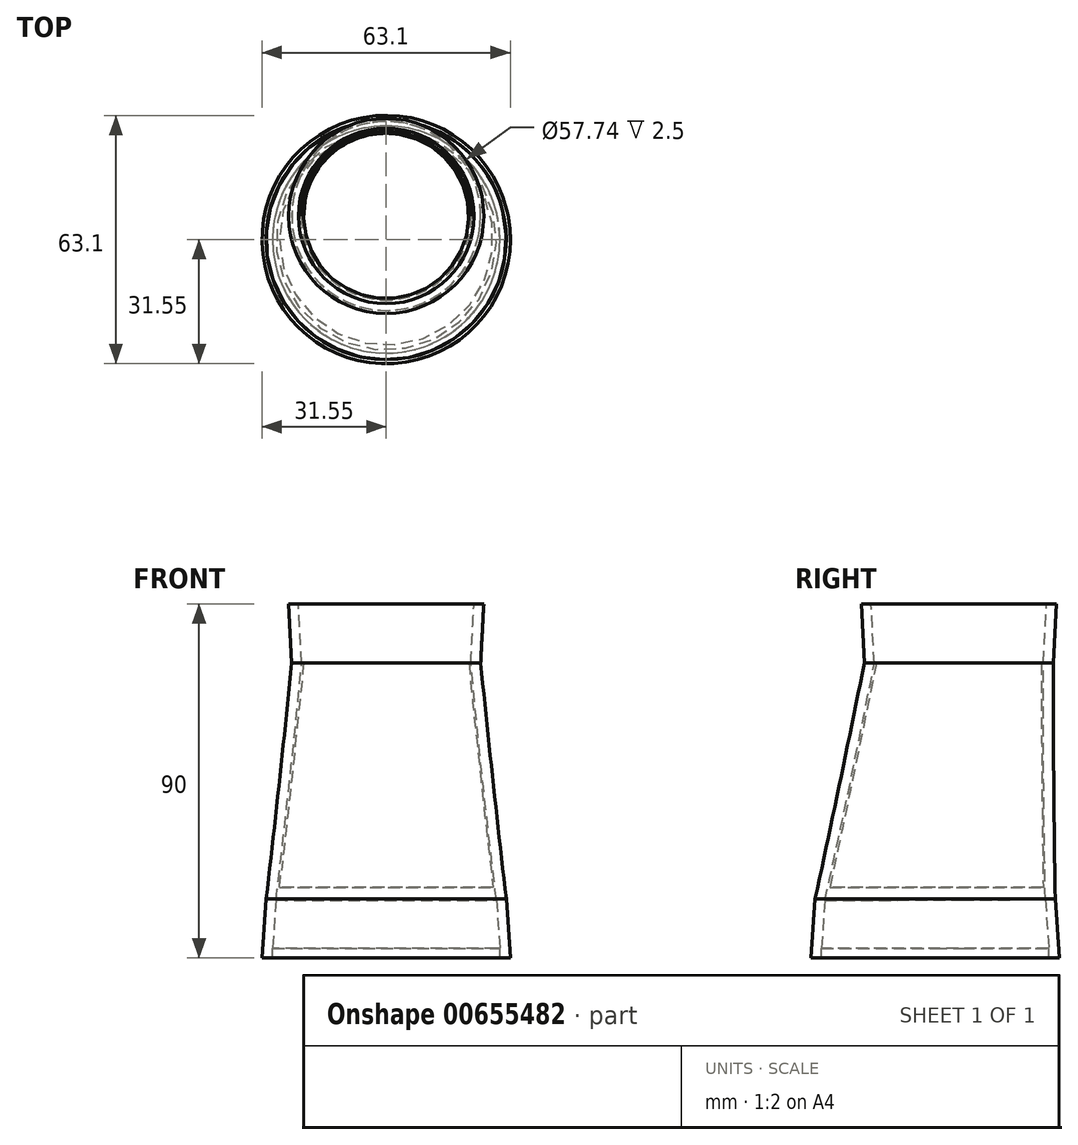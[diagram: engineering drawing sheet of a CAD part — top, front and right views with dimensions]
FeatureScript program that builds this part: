
annotation { "Feature Type Name" : "Feature", "Feature Type Description" : "" }
export const myFeature = defineFeature(function(context is Context, id is Id, definition is map)
    precondition{}
    {
        {
            var Q0;
            Q0=qCreatedBy(makeId("Top.planeOp"),FACE);
            var sketch = newSketch(context, id + "F0", { "sketchPlane" : qUnion([Q0])});
            skCircle(sketch, "E0", {"center": v(0, 0) * mm, "radius": 27.5 * mm, "construction": true});
            skCircle(sketch, "E1.0", {"center": v(0, 0) * mm, "radius": 30.5 * mm});
            skSolve(sketch);
        }
        {
            var Q0;
            Q0=qCreatedBy(makeId("Top.planeOp"),FACE);
            cPlane(context, id + "F1", {"entities" : qUnion([Q0]), "cplaneType" : CPlaneType.OFFSET, "offset" : 60 * mm, "width" : 150 * mm, "height" : 150 * mm});
        }
        {
            var Q0;
            Q0=qCreatedBy(id+"F1.planeOp",FACE);
            var sketch = newSketch(context, id + "F2", { "sketchPlane" : qUnion([Q0])});
            skCircle(sketch, "E2", {"center": v(0, 6.01) * mm, "radius": 21 * mm, "construction": true});
            skCircle(sketch, "E3.0", {"center": v(0, 6.01) * mm, "radius": 24 * mm});
            skSolve(sketch);
        }
        {
            var Q0;
            Q0=makeQuery(id+"F2.imprint","IMPRINT",FACE,{"disambiguationData":[TD([[makeQuery(id+"F2.imprint","IMPRINT",EDGE,{"derivedFrom":sQuery(id+"F2.wireOp",EDGE,"E3.0")}),1.0]])]});
            extrude(context, id + "F3", {"entities" : qUnion([Q0]), "depth" : 15 * mm, "offsetDistance" : 25 * mm, "hasDraft" : true, "draftAngle" : 3 * degree});
        }
        {
            var Q0;
            Q0=makeQuery(id+"F0.imprint","IMPRINT",FACE,{"disambiguationData":[TD([[makeQuery(id+"F0.imprint","IMPRINT",EDGE,{"derivedFrom":sQuery(id+"F0.wireOp",EDGE,"E1.0")}),1.0]])]});
            extrude(context, id + "F4", {"entities" : qUnion([Q0]), "oppositeDirection" : true, "depth" : 15 * mm, "offsetDistance" : 25 * mm, "hasDraft" : true, "draftAngle" : 4 * degree});
        }
        {
            var Q0;
            Q0 = qSketchRegion(id + "F2", true);
            var Q1;
            Q1 = qSketchRegion(id + "F0", true);
            loft(context, id + "F5", {"operationType" : NewBodyOperationType.ADD, "sheetProfilesArray" : [{ "sheetProfileEntities" : qUnion([Q0]) }, { "sheetProfileEntities" : qUnion([Q1]) }]});
        }
        {
            var Q0;
            Q0=makeQuery(id+"F3.opExtrude","CAP_FACE",FACE,{"disambiguationData":[OSD([sQuery(id+"F2.wireOp",EDGE,"E3.0")])],"isStart":false});
            shell(context, id + "F6", {"entities" : qUnion([Q0]), "thickness" : 2.5 * mm});
        }
        {
            var Q0;
            {var subQ0=sQuery(id+"F0.wireOp",EDGE,"E1.0");Q0=makeQuery(id+"F6.opShell","OFFSET_FACE",FACE,{"disambiguationData":[OSD([subQ0]),TDD([makeQuery(id+"F4.opExtrude","CAP_FACE",FACE,{"disambiguationData":[OSD([subQ0])],"isStart":false})])]});}
            var sketch = newSketch(context, id + "F7", { "sketchPlane" : qUnion([Q0])});
            skCircle(sketch, "E4.0", {"center": v(0, 0) * mm, "radius": 28.87 * mm});
            skSolve(sketch);
        }
        {
            var Q0;
            Q0 = qSketchRegion(id + "F7", true);
            extrude(context, id + "F8", {"entities" : qUnion([Q0]), "operationType" : NewBodyOperationType.REMOVE, "oppositeDirection" : true, "depth" : 25 * mm, "offsetDistance" : 25 * mm});
        }
        {
            var Q0;
            Q0=makeQuery(id+"F0.imprint","IMPRINT",FACE,{"disambiguationData":[TD([[makeQuery(id+"F0.imprint","IMPRINT",EDGE,{"derivedFrom":sQuery(id+"F0.wireOp",EDGE,"E1.0")}),1.0]])]});
            var Q1;
            Q1=makeQuery(id+"F2.imprint","IMPRINT",FACE,{"disambiguationData":[TD([[makeQuery(id+"F2.imprint","IMPRINT",EDGE,{"derivedFrom":sQuery(id+"F2.wireOp",EDGE,"E3.0")}),1.0]])]});
            loft(context, id + "F9", {"sheetProfilesArray" : [{ "sheetProfileEntities" : qUnion([Q0]) }, { "sheetProfileEntities" : qUnion([Q1]) }]});
        }
        {
            var Q0;
            Q0=makeQuery(id+"F9.opLoft","CAP_FACE",FACE,{"disambiguationData":[OSD([makeQuery(id+"F2.imprint","IMPRINT",FACE,{"disambiguationData":[TD([[makeQuery(id+"F2.imprint","IMPRINT",EDGE,{"derivedFrom":sQuery(id+"F2.wireOp",EDGE,"E3.0")}),1.0]])]})])],"isStart":true});
            shell(context, id + "F10", {"entities" : qUnion([Q0]), "thickness" : 3 * mm});
        }
    });
